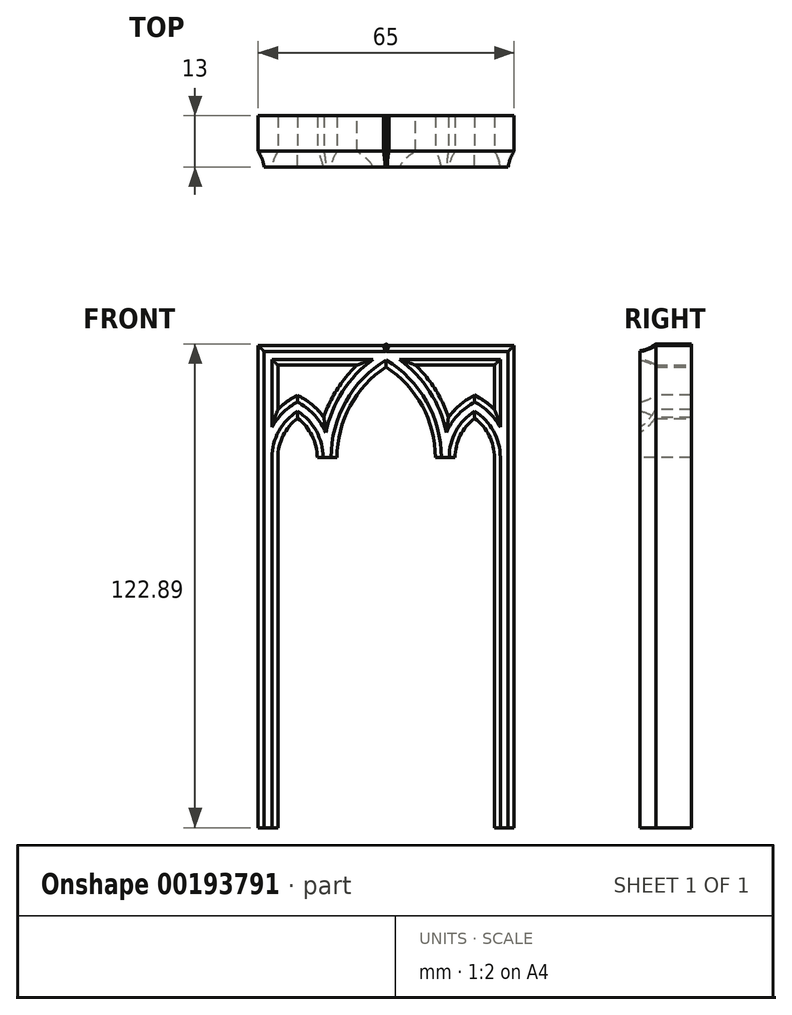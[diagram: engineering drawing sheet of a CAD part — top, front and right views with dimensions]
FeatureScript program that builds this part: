
annotation { "Feature Type Name" : "Feature", "Feature Type Description" : "" }
export const myFeature = defineFeature(function(context is Context, id is Id, definition is map)
    precondition{}
    {
        {
            var Q0;
            Q0=qCreatedBy(makeId("Front.planeOp"),FACE);
            var sketch = newSketch(context, id + "F0", { "sketchPlane" : qUnion([Q0])});
            skLineSegment(sketch, "E0", {"start": v(0, 0) * mm, "end": v(-15, 0) * mm, "construction": true});
            skLineSegment(sketch, "E1", {"start": v(-15, 0) * mm, "end": v(-30, 0) * mm, "construction": true});
            skLineSegment(sketch, "E2", {"start": v(0, 0) * mm, "end": v(15, 0) * mm, "construction": true});
            skLineSegment(sketch, "E3", {"start": v(15, 0) * mm, "end": v(30, 0) * mm, "construction": true});
            skLineSegment(sketch, "E4", {"start": v(-30, 0) * mm, "end": v(-30, 94.02) * mm});
            skLineSegment(sketch, "E5", {"start": v(-30, 120) * mm, "end": v(-15, 120) * mm});
            skLineSegment(sketch, "E6", {"start": v(30, 120) * mm, "end": v(30, 0) * mm});
            skLineSegment(sketch, "E7", {"start": v(-15, 0) * mm, "end": v(-15, 120) * mm, "construction": true});
            skLineSegment(sketch, "E8", {"start": v(15, 0) * mm, "end": v(15, 120) * mm, "construction": true});
            skLineSegment(sketch, "E9", {"start": v(-15, 120) * mm, "end": v(15, 120) * mm});
            skLineSegment(sketch, "E10", {"start": v(15, 120) * mm, "end": v(30, 120) * mm});
            skLineSegment(sketch, "E11", {"start": v(-15, 94.02) * mm, "end": v(-30, 94.02) * mm, "construction": true});
            skLineSegment(sketch, "E12", {"start": v(-15, 94.02) * mm, "end": v(15, 94.02) * mm, "construction": true});
            skLineSegment(sketch, "E13", {"start": v(15, 94.02) * mm, "end": v(30, 94.02) * mm, "construction": true});
            skArc(sketch, "E14", {"start": v(-15, 94.02) * mm, "mid": v(-10.98, 109.02) * mm, "end": v(0, 120) * mm});
            skArc(sketch, "E15", {"start": v(0, 120) * mm, "mid": v(10.98, 109.02) * mm, "end": v(15, 94.02) * mm});
            skArc(sketch, "E16", {"start": v(15, 94.02) * mm, "mid": v(17, 101.52) * mm, "end": v(22.5, 107) * mm});
            skArc(sketch, "E17", {"start": v(30, 94.02) * mm, "mid": v(28, 101.52) * mm, "end": v(22.5, 107) * mm});
            skArc(sketch, "E18", {"start": v(-15, 94.02) * mm, "mid": v(-17, 101.52) * mm, "end": v(-22.5, 107) * mm});
            skArc(sketch, "E19", {"start": v(-30, 94.02) * mm, "mid": v(-28, 101.52) * mm, "end": v(-22.5, 107) * mm});
            skArc(sketch, "E20", {"start": v(-22.5, 107) * mm, "mid": v(-26.12, 108.5) * mm, "end": v(-30, 109.02) * mm, "construction": true});
            skArc(sketch, "E21", {"start": v(22.5, 107) * mm, "mid": v(26.12, 108.5) * mm, "end": v(30, 109.02) * mm, "construction": true});
            skArc(sketch, "E22", {"start": v(0, 94.02) * mm, "mid": v(-1.94, 104.63) * mm, "end": v(-7.5, 113.86) * mm});
            skArc(sketch, "E23", {"start": v(-7.5, 113.86) * mm, "mid": v(-11, 117.24) * mm, "end": v(-15, 120) * mm, "construction": true});
            skArc(sketch, "E24", {"start": v(0, 94.02) * mm, "mid": v(1.94, 104.63) * mm, "end": v(7.5, 113.86) * mm});
            skArc(sketch, "E25", {"start": v(15, 120) * mm, "mid": v(11, 117.24) * mm, "end": v(7.5, 113.86) * mm, "construction": true});
            skLineSegment(sketch, "E26", {"start": v(-30, 94.02) * mm, "end": v(-30, 120) * mm});
            skSolve(sketch);
        }
        {
            var Q0;
            Q0=qCreatedBy(makeId("Top.planeOp"),FACE);
            var sketch = newSketch(context, id + "F1", { "sketchPlane" : qUnion([Q0])});
            skLineSegment(sketch, "E27.bottom", {"start": v(-32.5, 6.5) * mm, "end": v(-27.5, 6.5) * mm});
            skLineSegment(sketch, "E27.top", {"start": v(-32.5, -6.5) * mm, "end": v(-27.5, -6.5) * mm});
            skLineSegment(sketch, "E27.left", {"start": v(-32.5, 6.5) * mm, "end": v(-32.5, -6.5) * mm});
            skLineSegment(sketch, "E27.right", {"start": v(-27.5, 6.5) * mm, "end": v(-27.5, -6.5) * mm});
            skPoint(sketch, "E28", {"position": v(-32.5, -2.5) * mm});
            skPoint(sketch, "E29", {"position": v(-31, -6.5) * mm});
            skPoint(sketch, "E30", {"position": v(-29, -6.5) * mm});
            skPoint(sketch, "E31", {"position": v(-27.5, -2.5) * mm});
            skArc(sketch, "E32", {"start": v(-31, -6.5) * mm, "mid": v(-31.53, -4.42) * mm, "end": v(-32.5, -2.5) * mm});
            skArc(sketch, "E33", {"start": v(-27.5, -2.5) * mm, "mid": v(-28.47, -4.42) * mm, "end": v(-29, -6.5) * mm});
            skSolve(sketch);
        }
        {
            var Q0;
            {var subQ1=sQuery(id+"F1.wireOp",EDGE,"E27.bottom");Q0=makeQuery(id+"F1.imprint","IMPRINT",FACE,{"disambiguationData":[TD([[makeQuery(id+"F1.imprint","IMPRINT",EDGE,{"derivedFrom":subQ1}),-1.0]])]});}
            var Q1;
            Q1=sQuery(id+"F0.wireOp",EDGE,"E4");
            var Q2;
            Q2=sQuery(id+"F0.wireOp",EDGE,"E5");
            var Q3;
            Q3=sQuery(id+"F0.wireOp",EDGE,"E9");
            var Q4;
            Q4=sQuery(id+"F0.wireOp",EDGE,"E10");
            var Q5;
            Q5=sQuery(id+"F0.wireOp",EDGE,"E6");
            var Q6;
            Q6=sQuery(id+"F0.wireOp",EDGE,"E26");
            sweep(context, id + "F2", {"profiles" : qUnion([Q0]), "path" : qUnion([Q1, Q2, Q3, Q4, Q5, Q6])});
        }
        {
            var Q0;
            {var subQ1=sQuery(id+"F1.wireOp",EDGE,"E27.bottom");Q0=makeQuery(id+"F1.imprint","IMPRINT",FACE,{"disambiguationData":[TD([[makeQuery(id+"F1.imprint","IMPRINT",EDGE,{"derivedFrom":subQ1}),-1.0]])]});}
            var Q1;
            Q1=sQuery(id+"F0.wireOp",EDGE,"E19");
            var Q2;
            Q2=sQuery(id+"F0.wireOp",EDGE,"E4");
            var Q3;
            Q3=sQuery(id+"F0.wireOp",EDGE,"E18");
            sweep(context, id + "F3", {"operationType" : NewBodyOperationType.ADD, "profiles" : qUnion([Q0]), "path" : qUnion([Q1, Q2, Q3])});
        }
        {
            var Q0;
            Q0=makeQuery(id+"F3.opSweep","CAP_FACE",FACE,{"disambiguationData":[OSD([sQuery(id+"F0.wireOp",VERTEX,"E18.start"),sQuery(id+"F1.wireOp",EDGE,"E27.bottom"),sQuery(id+"F1.wireOp",EDGE,"E27.top"),sQuery(id+"F1.wireOp",EDGE,"E27.left"),sQuery(id+"F1.wireOp",EDGE,"E27.right"),sQuery(id+"F1.wireOp",EDGE,"E32"),sQuery(id+"F1.wireOp",EDGE,"E33")])],"isStart":false});
            var Q1;
            Q1=sQuery(id+"F0.wireOp",EDGE,"E14");
            var Q2;
            Q2=sQuery(id+"F0.wireOp",EDGE,"E15");
            sweep(context, id + "F4", {"operationType" : NewBodyOperationType.ADD, "profiles" : qUnion([Q0]), "path" : qUnion([Q1, Q2])});
        }
        {
            var Q0;
            Q0=makeQuery(id+"F4.opSweep","CAP_FACE",FACE,{"disambiguationData":[OSD([sQuery(id+"F0.wireOp",VERTEX,"E15.end"),sQuery(id+"F0.wireOp",VERTEX,"E18.start"),sQuery(id+"F1.wireOp",EDGE,"E27.bottom"),sQuery(id+"F1.wireOp",EDGE,"E27.top"),sQuery(id+"F1.wireOp",EDGE,"E27.left"),sQuery(id+"F1.wireOp",EDGE,"E27.right"),sQuery(id+"F1.wireOp",EDGE,"E32"),sQuery(id+"F1.wireOp",EDGE,"E33")])],"isStart":false});
            var Q1;
            Q1=sQuery(id+"F0.wireOp",EDGE,"E16");
            var Q2;
            Q2=sQuery(id+"F0.wireOp",EDGE,"E17");
            sweep(context, id + "F5", {"operationType" : NewBodyOperationType.ADD, "profiles" : qUnion([Q0]), "path" : qUnion([Q1, Q2])});
        }
    });
